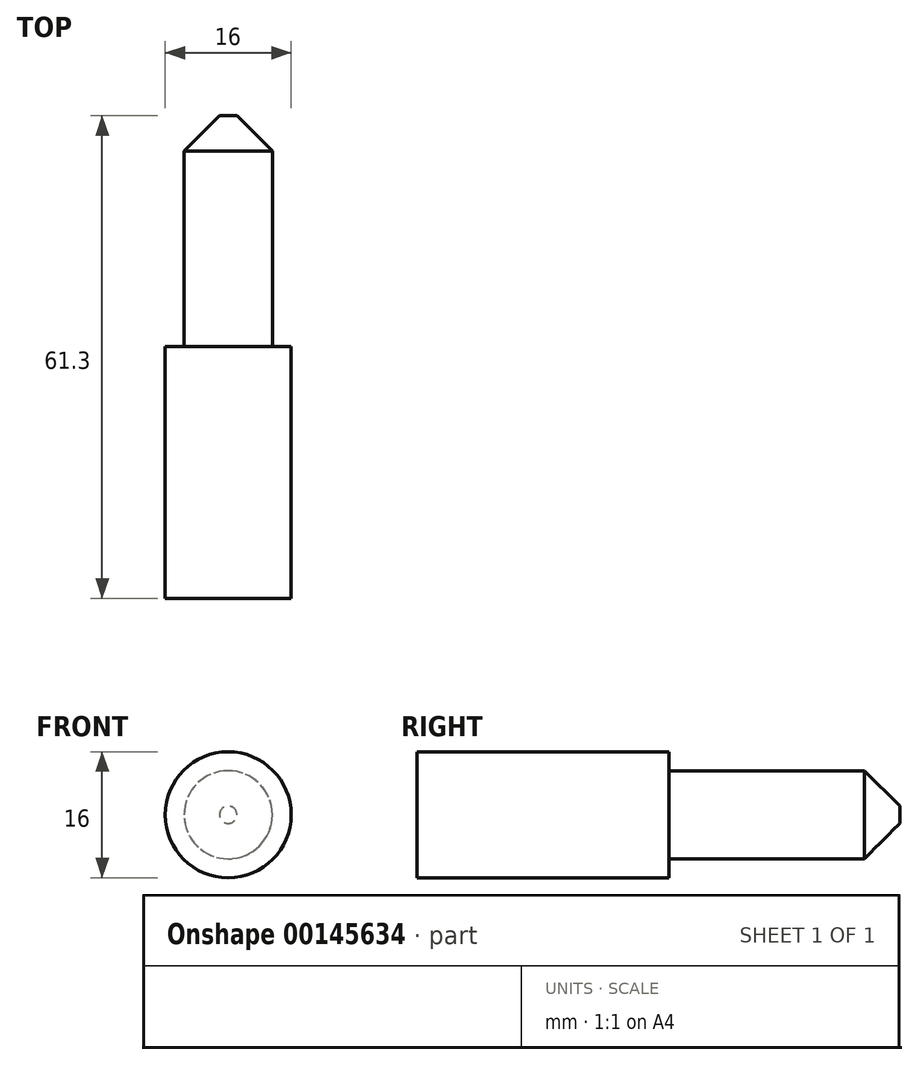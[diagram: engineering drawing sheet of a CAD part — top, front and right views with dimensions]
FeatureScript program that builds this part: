
annotation { "Feature Type Name" : "Feature", "Feature Type Description" : "" }
export const myFeature = defineFeature(function(context is Context, id is Id, definition is map)
    precondition{}
    {
        {
            var Q0;
            Q0=qCreatedBy(makeId("Right.planeOp"),FACE);
            var sketch = newSketch(context, id + "F0", { "sketchPlane" : qUnion([Q0])});
            skLineSegment(sketch, "E0", {"start": v(0, 0) * mm, "end": v(0, 8) * mm});
            skLineSegment(sketch, "E1", {"start": v(0, 8) * mm, "end": v(32, 8) * mm});
            skLineSegment(sketch, "E2", {"start": v(32, 8) * mm, "end": v(32, 5.6) * mm});
            skLineSegment(sketch, "E3", {"start": v(32, 5.6) * mm, "end": v(61.3, 5.6) * mm});
            skLineSegment(sketch, "E4", {"start": v(61.3, 5.6) * mm, "end": v(61.3, 0) * mm});
            skLineSegment(sketch, "E5", {"start": v(61.3, 0) * mm, "end": v(0, 0) * mm});
            skSolve(sketch);
        }
        {
            var Q0;
            Q0=makeQuery(id+"F0.imprint","IMPRINT",FACE,{"disambiguationData":[TD([[makeQuery(id+"F0.imprint","IMPRINT",EDGE,{"derivedFrom":sQuery(id+"F0.wireOp",EDGE,"E0")}),-1.0]])]});
            var Q1;
            Q1=sQuery(id+"F0.wireOp",EDGE,"E5");
            revolve(context, id + "F1", {"entities" : qUnion([Q0]), "axis" : qUnion([Q1]), "revolveType" : RevolveType.FULL});
        }
        {
            var Q0;
            Q0=makeQuery(id+"F1.opRevolve","SWEPT_EDGE",EDGE,{"disambiguationData":[OSD([sQuery(id+"F0.wireOp",EDGE,"E3"),sQuery(id+"F0.wireOp",EDGE,"E4")])]});
            chamfer(context, id + "F2", {"entities" : qUnion([Q0]), "width" : 4.5 * mm, "tangentPropagation" : true});
        }
    });
